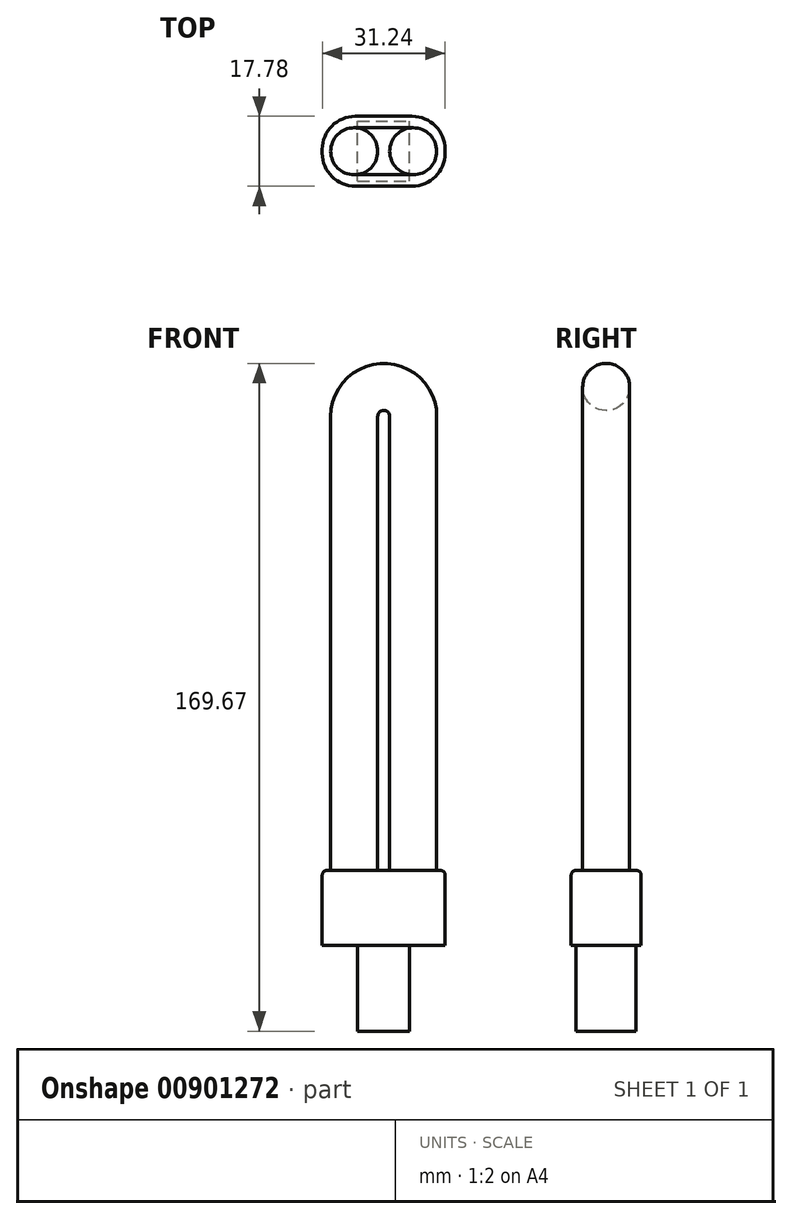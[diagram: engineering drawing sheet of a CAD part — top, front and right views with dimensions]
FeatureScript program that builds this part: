
annotation { "Feature Type Name" : "Feature", "Feature Type Description" : "" }
export const myFeature = defineFeature(function(context is Context, id is Id, definition is map)
    precondition{}
    {
        {
            var Q0;
            Q0=qCreatedBy(makeId("Top.planeOp"),FACE);
            var sketch = newSketch(context, id + "F0", { "sketchPlane" : qUnion([Q0])});
            skCircle(sketch, "E0", {"center": v(7.5, 0) * mm, "radius": 5.97 * mm});
            skCircle(sketch, "E1", {"center": v(-7.5, 0) * mm, "radius": 5.97 * mm});
            skSolve(sketch);
        }
        {
            var Q0;
            Q0=qSketchRegion(id+"F0",true);
            extrude(context, id + "F1", {"entities" : qUnion([Q0]), "depth" : 115.32 * mm, "offsetDistance" : 25.4 * mm});
        }
        {
            var Q0;
            Q0=qCreatedBy(makeId("Top.planeOp"),FACE);
            var sketch = newSketch(context, id + "F2", { "sketchPlane" : qUnion([Q0])});
            skLineSegment(sketch, "E2.bottom", {"start": v(-7.24, -8.9) * mm, "end": v(7.24, -8.9) * mm});
            skLineSegment(sketch, "E2.top", {"start": v(-7.24, 8.9) * mm, "end": v(7.24, 8.9) * mm});
            skLineSegment(sketch, "E2.left", {"start": v(-15.62, -0.5) * mm, "end": v(-15.62, 0.5) * mm});
            skLineSegment(sketch, "E2.right", {"start": v(15.62, -0.5) * mm, "end": v(15.62, 0.5) * mm});
            skPoint(sketch, "E2.middle", {"position": v(0, 0) * mm});
            skPoint(sketch, "E3.visualSharp", {"position": v(-15.62, -8.9) * mm});
            skArc(sketch, "E3.filletArc", {"start": v(-15.62, -0.5) * mm, "mid": v(-13.17, -6.43) * mm, "end": v(-7.24, -8.9) * mm});
            skPoint(sketch, "E4.visualSharp", {"position": v(-15.62, 8.9) * mm});
            skArc(sketch, "E4.filletArc", {"start": v(-7.24, 8.9) * mm, "mid": v(-13.17, 6.43) * mm, "end": v(-15.62, 0.5) * mm});
            skPoint(sketch, "E5.visualSharp", {"position": v(15.62, -8.9) * mm});
            skArc(sketch, "E5.filletArc", {"start": v(7.24, -8.9) * mm, "mid": v(13.17, -6.43) * mm, "end": v(15.62, -0.5) * mm});
            skPoint(sketch, "E6.visualSharp", {"position": v(15.62, 8.9) * mm});
            skArc(sketch, "E6.filletArc", {"start": v(15.62, 0.5) * mm, "mid": v(13.17, 6.43) * mm, "end": v(7.24, 8.9) * mm});
            skSolve(sketch);
        }
        {
            var Q0;
            Q0=qSketchRegion(id+"F2",true);
            extrude(context, id + "F3", {"entities" : qUnion([Q0]), "operationType" : NewBodyOperationType.ADD, "oppositeDirection" : true, "depth" : 19.05 * mm, "offsetDistance" : 25.4 * mm});
        }
        {
            var Q0;
            Q0=makeQuery(id+"F1.opExtrude","CAP_FACE",FACE,{"disambiguationData":[OSD([sQuery(id+"F0.wireOp",EDGE,"E1")])],"isStart":false});
            var sketch = newSketch(context, id + "F4", { "sketchPlane" : qUnion([Q0])});
            skLineSegment(sketch, "E7", {"start": v(0, 0) * mm, "end": v(0, 42.09) * mm, "construction": true});
            skSolve(sketch);
        }
        {
            var Q0;
            Q0=makeQuery(id+"F1.opExtrude","CAP_FACE",FACE,{"disambiguationData":[OSD([sQuery(id+"F0.wireOp",EDGE,"E0")])],"isStart":false});
            var Q1;
            Q1=sQuery(id+"F4.wireOp",EDGE,"E7");
            revolve(context, id + "F5", {"operationType" : NewBodyOperationType.ADD, "surfaceOperationType" : NewSurfaceOperationType.NEW, "entities" : qUnion([Q0]), "axis" : qUnion([Q1]), "revolveType" : RevolveType.ONE_DIRECTION, "oppositeDirection" : true, "angle" : 180 * degree});
        }
        {
            var Q0;
            Q0=makeQuery(id+"F3.opExtrude","CAP_EDGE",EDGE,{"disambiguationData":[OSD([sQuery(id+"F2.wireOp",EDGE,"E2.bottom")])],"isStart":true});
            fillet(context, id + "F6", {"entities" : qUnion([Q0]), "radius" : 1.27 * mm, "tangentPropagation" : true, "allowEdgeOverflow" : false});
        }
        {
            var Q0;
            Q0=makeQuery(id+"F3.opExtrude","CAP_FACE",FACE,{"disambiguationData":[OSD([sQuery(id+"F2.wireOp",EDGE,"E2.bottom"),sQuery(id+"F2.wireOp",EDGE,"E2.top"),sQuery(id+"F2.wireOp",EDGE,"E2.left"),sQuery(id+"F2.wireOp",EDGE,"E2.right"),sQuery(id+"F2.wireOp",EDGE,"E3.filletArc"),sQuery(id+"F2.wireOp",EDGE,"E4.filletArc"),sQuery(id+"F2.wireOp",EDGE,"E5.filletArc"),sQuery(id+"F2.wireOp",EDGE,"E6.filletArc")])],"isStart":false});
            var sketch = newSketch(context, id + "F7", { "sketchPlane" : qUnion([Q0])});
            skLineSegment(sketch, "E8.bottom", {"start": v(-6.6, 7.62) * mm, "end": v(6.6, 7.62) * mm});
            skLineSegment(sketch, "E8.top", {"start": v(-6.6, -7.62) * mm, "end": v(6.6, -7.62) * mm});
            skLineSegment(sketch, "E8.left", {"start": v(-6.6, 7.62) * mm, "end": v(-6.6, -7.62) * mm});
            skLineSegment(sketch, "E8.right", {"start": v(6.6, 7.62) * mm, "end": v(6.6, -7.62) * mm});
            skPoint(sketch, "E8.middle", {"position": v(0, 0) * mm});
            skSolve(sketch);
        }
        {
            var Q0;
            Q0 = qSketchRegion(id + "F7", true);
            extrude(context, id + "F8", {"entities" : qUnion([Q0]), "operationType" : NewBodyOperationType.ADD, "depth" : 21.84 * mm, "offsetDistance" : 25.4 * mm});
        }
    });
